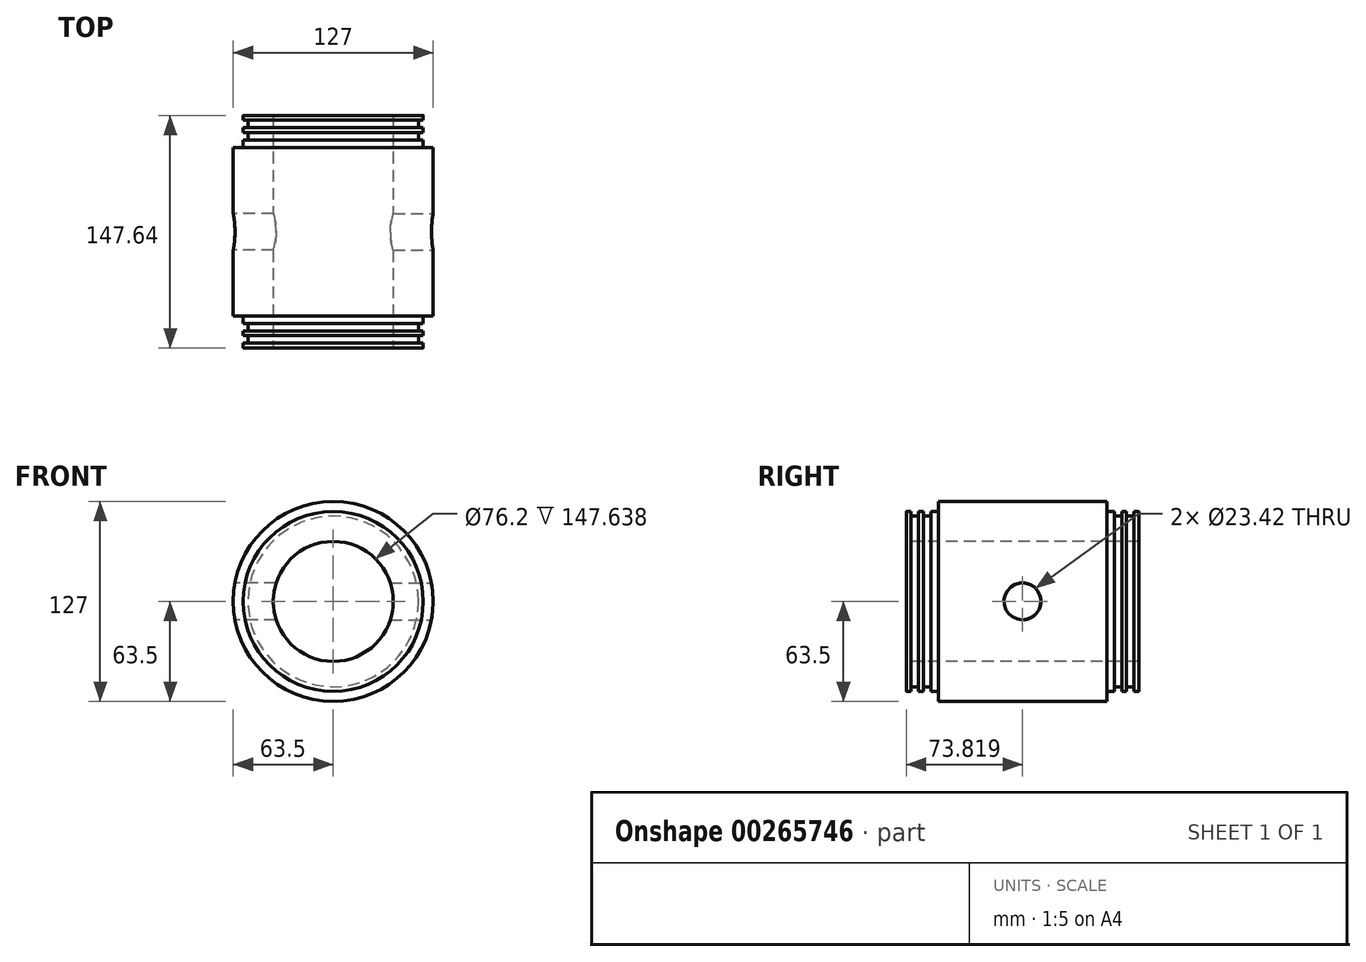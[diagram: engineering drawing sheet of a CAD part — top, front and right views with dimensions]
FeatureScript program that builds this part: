
annotation { "Feature Type Name" : "Feature", "Feature Type Description" : "" }
export const myFeature = defineFeature(function(context is Context, id is Id, definition is map)
    precondition{}
    {
        {
            var Q0;
            Q0=qCreatedBy(makeId("Right.planeOp"),FACE);
            var sketch = newSketch(context, id + "F0", { "sketchPlane" : qUnion([Q0])});
            skLineSegment(sketch, "E0", {"start": v(0, 0) * mm, "end": v(0, 57.15) * mm});
            skLineSegment(sketch, "E1", {"start": v(0, 57.15) * mm, "end": v(20.32, 57.15) * mm});
            skLineSegment(sketch, "E2", {"start": v(20.32, 57.15) * mm, "end": v(20.32, 63.5) * mm});
            skLineSegment(sketch, "E3", {"start": v(20.32, 63.5) * mm, "end": v(127.32, 63.5) * mm});
            skLineSegment(sketch, "E4", {"start": v(127.32, 63.5) * mm, "end": v(127.32, 57.15) * mm});
            skLineSegment(sketch, "E5", {"start": v(127.32, 57.15) * mm, "end": v(147.64, 57.15) * mm});
            skLineSegment(sketch, "E6", {"start": v(147.64, 57.15) * mm, "end": v(147.64, 0) * mm});
            skLineSegment(sketch, "E7", {"start": v(0, 0) * mm, "end": v(147.64, 0) * mm});
            skLineSegment(sketch, "E8", {"start": v(0, 57.15) * mm, "end": v(3.05, 57.15) * mm});
            skLineSegment(sketch, "E9", {"start": v(3.05, 57.15) * mm, "end": v(3.05, 54.15) * mm});
            skLineSegment(sketch, "E10", {"start": v(3.05, 54.15) * mm, "end": v(7.8, 54.15) * mm});
            skLineSegment(sketch, "E11", {"start": v(7.8, 54.15) * mm, "end": v(7.8, 57.15) * mm});
            skLineSegment(sketch, "E12", {"start": v(7.8, 57.15) * mm, "end": v(10.8, 57.15) * mm});
            skLineSegment(sketch, "E13", {"start": v(10.8, 57.15) * mm, "end": v(10.8, 54.15) * mm});
            skLineSegment(sketch, "E14", {"start": v(10.8, 54.15) * mm, "end": v(15.54, 54.15) * mm});
            skLineSegment(sketch, "E15", {"start": v(15.54, 54.15) * mm, "end": v(15.54, 57.15) * mm});
            skLineSegment(sketch, "E16", {"start": v(15.54, 57.15) * mm, "end": v(20.32, 57.15) * mm});
            skLineSegment(sketch, "E17", {"start": v(147.64, 57.15) * mm, "end": v(144.59, 57.15) * mm});
            skLineSegment(sketch, "E18", {"start": v(144.59, 57.15) * mm, "end": v(144.59, 54.15) * mm});
            skLineSegment(sketch, "E19", {"start": v(144.59, 54.15) * mm, "end": v(139.84, 54.15) * mm});
            skLineSegment(sketch, "E20", {"start": v(139.84, 54.15) * mm, "end": v(139.84, 57.15) * mm});
            skLineSegment(sketch, "E21", {"start": v(139.84, 57.15) * mm, "end": v(136.84, 57.15) * mm});
            skLineSegment(sketch, "E22", {"start": v(136.84, 57.15) * mm, "end": v(136.84, 54.15) * mm});
            skLineSegment(sketch, "E23", {"start": v(136.84, 54.15) * mm, "end": v(132.1, 54.15) * mm});
            skLineSegment(sketch, "E24", {"start": v(132.1, 54.15) * mm, "end": v(132.1, 57.15) * mm});
            skSolve(sketch);
        }
        {
            var Q0;
            Q0=makeQuery(id+"F0.imprint","IMPRINT",FACE,{"disambiguationData":[TD([[makeQuery(id+"F0.imprint","IMPRINT",EDGE,{"derivedFrom":sQuery(id+"F0.wireOp",EDGE,"E0")}),-1.0]])]});
            var Q1;
            Q1=sQuery(id+"F0.wireOp",EDGE,"E7");
            revolve(context, id + "F1", {"entities" : qUnion([Q0]), "axis" : qUnion([Q1]), "revolveType" : RevolveType.FULL});
        }
        {
            var Q0;
            Q0=makeQuery(id+"F1.opRevolve","SWEPT_FACE",FACE,{"disambiguationData":[OSD([sQuery(id+"F0.wireOp",EDGE,"E0")])]});
            var sketch = newSketch(context, id + "F2", { "sketchPlane" : qUnion([Q0])});
            skCircle(sketch, "E25", {"center": v(0, 0) * mm, "radius": 38.1 * mm});
            skSolve(sketch);
        }
        {
            var Q0;
            Q0=makeQuery(id+"F2.imprint","IMPRINT",FACE,{"disambiguationData":[TD([[makeQuery(id+"F2.imprint","IMPRINT",EDGE,{"derivedFrom":sQuery(id+"F2.wireOp",EDGE,"E25")}),1.0]])]});
            extrude(context, id + "F3", {"entities" : qUnion([Q0]), "operationType" : NewBodyOperationType.REMOVE, "endBound" : BoundingType.UP_TO_NEXT, "oppositeDirection" : true, "depth" : 25.4 * mm});
        }
        {
            var Q0;
            Q0=makeQuery(id+"F1.opRevolve","SWEPT_EDGE",EDGE,{"disambiguationData":[OSD([sQuery(id+"F0.wireOp",EDGE,"E0"),sQuery(id+"F0.wireOp",EDGE,"E8")])]});
            var Q1;
            Q1=makeQuery(id+"F1.opRevolve","SWEPT_EDGE",EDGE,{"disambiguationData":[OSD([sQuery(id+"F0.wireOp",EDGE,"E6"),sQuery(id+"F0.wireOp",EDGE,"E17")])]});
            fillet(context, id + "F4", {"entities" : qUnion([Q0, Q1]), "radius" : 0.13 * mm, "tangentPropagation" : true, "allowEdgeOverflow" : false});
        }
        {
            var Q0;
            Q0=qCreatedBy(makeId("Right.planeOp"),FACE);
            cPlane(context, id + "F5", {"entities" : qUnion([Q0]), "cplaneType" : CPlaneType.OFFSET, "offset" : 63.5 * mm, "width" : 152.4 * mm, "height" : 152.4 * mm});
        }
        {
            var Q0;
            Q0=qCreatedBy(id+"F5.planeOp",FACE);
            var sketch = newSketch(context, id + "F6", { "sketchPlane" : qUnion([Q0])});
            skPoint(sketch, "E26", {"position": v(73.82, 0) * mm});
            skSolve(sketch);
        }
        {
            var Q0;
            Q0=sQuery(id+"F6.wireOp",VERTEX,"E26");
            var Q1;
            Q1=makeQuery(id+"F1.opRevolve","SWEPT_BODY",BODY,{"disambiguationData":[OSD([sQuery(id+"F0.wireOp",EDGE,"E0"),sQuery(id+"F0.wireOp",EDGE,"E2"),sQuery(id+"F0.wireOp",EDGE,"E3"),sQuery(id+"F0.wireOp",EDGE,"E4"),sQuery(id+"F0.wireOp",EDGE,"E5"),sQuery(id+"F0.wireOp",EDGE,"E6"),sQuery(id+"F0.wireOp",EDGE,"E7"),sQuery(id+"F0.wireOp",EDGE,"E8"),sQuery(id+"F0.wireOp",EDGE,"E9"),sQuery(id+"F0.wireOp",EDGE,"E10"),sQuery(id+"F0.wireOp",EDGE,"E11"),sQuery(id+"F0.wireOp",EDGE,"E12"),sQuery(id+"F0.wireOp",EDGE,"E13"),sQuery(id+"F0.wireOp",EDGE,"E14"),sQuery(id+"F0.wireOp",EDGE,"E15"),sQuery(id+"F0.wireOp",EDGE,"E16"),sQuery(id+"F0.wireOp",EDGE,"E17"),sQuery(id+"F0.wireOp",EDGE,"E18"),sQuery(id+"F0.wireOp",EDGE,"E19"),sQuery(id+"F0.wireOp",EDGE,"E20"),sQuery(id+"F0.wireOp",EDGE,"E21"),sQuery(id+"F0.wireOp",EDGE,"E22"),sQuery(id+"F0.wireOp",EDGE,"E23"),sQuery(id+"F0.wireOp",EDGE,"E24")])]});
            hole(context, id + "F7", {"style" : HoleStyle.SIMPLE, "endStyle" : HoleEndStyle.BLIND, "standardTappedOrClearance" : lookupTablePath({ "standard" : "ANSI", "engagement" : "75%", "pitch" : "12 tpi", "size" : "1", "type" : "Tapped" }), "standardBlindInLast" : lookupTablePath({ "standard" : "ANSI", "engagement" : "75%", "pitch" : "12 tpi", "size" : "1", "type" : "Tapped" }), "holeDiameter" : 23.42 * mm, "showTappedDepth" : true, "holeDepth" : 38.1 * mm, "tappedDepth" : 31.75 * mm, "tapClearance" : 3, "locations" : qUnion([Q0]), "scope" : qUnion([Q1]), "majorDiameter" : 25.4 * mm});
        }
        {
            var Q0;
            Q0=qCreatedBy(makeId("Right.planeOp"),FACE);
            cPlane(context, id + "F8", {"entities" : qUnion([Q0]), "cplaneType" : CPlaneType.OFFSET, "offset" : 63.5 * mm, "oppositeDirection" : true, "width" : 152.4 * mm, "height" : 152.4 * mm});
        }
        {
            var Q0;
            Q0=qCreatedBy(id+"F8.planeOp",FACE);
            var sketch = newSketch(context, id + "F9", { "sketchPlane" : qUnion([Q0])});
            skPoint(sketch, "E27", {"position": v(73.82, 0) * mm});
            skSolve(sketch);
        }
        {
            var Q0;
            Q0=sQuery(id+"F9.wireOp",VERTEX,"E27");
            var Q1;
            Q1=makeQuery(id+"F1.opRevolve","SWEPT_BODY",BODY,{"disambiguationData":[OSD([sQuery(id+"F0.wireOp",EDGE,"E0"),sQuery(id+"F0.wireOp",EDGE,"E2"),sQuery(id+"F0.wireOp",EDGE,"E3"),sQuery(id+"F0.wireOp",EDGE,"E4"),sQuery(id+"F0.wireOp",EDGE,"E5"),sQuery(id+"F0.wireOp",EDGE,"E6"),sQuery(id+"F0.wireOp",EDGE,"E7"),sQuery(id+"F0.wireOp",EDGE,"E8"),sQuery(id+"F0.wireOp",EDGE,"E9"),sQuery(id+"F0.wireOp",EDGE,"E10"),sQuery(id+"F0.wireOp",EDGE,"E11"),sQuery(id+"F0.wireOp",EDGE,"E12"),sQuery(id+"F0.wireOp",EDGE,"E13"),sQuery(id+"F0.wireOp",EDGE,"E14"),sQuery(id+"F0.wireOp",EDGE,"E15"),sQuery(id+"F0.wireOp",EDGE,"E16"),sQuery(id+"F0.wireOp",EDGE,"E17"),sQuery(id+"F0.wireOp",EDGE,"E18"),sQuery(id+"F0.wireOp",EDGE,"E19"),sQuery(id+"F0.wireOp",EDGE,"E20"),sQuery(id+"F0.wireOp",EDGE,"E21"),sQuery(id+"F0.wireOp",EDGE,"E22"),sQuery(id+"F0.wireOp",EDGE,"E23"),sQuery(id+"F0.wireOp",EDGE,"E24")])]});
            hole(context, id + "F10", {"style" : HoleStyle.SIMPLE, "endStyle" : HoleEndStyle.BLIND, "oppositeDirection" : true, "standardTappedOrClearance" : lookupTablePath({ "standard" : "ANSI", "engagement" : "75%", "pitch" : "12 tpi", "size" : "1", "type" : "Tapped" }), "standardBlindInLast" : lookupTablePath({ "standard" : "ANSI", "engagement" : "75%", "pitch" : "12 tpi", "size" : "1", "type" : "Tapped" }), "holeDiameter" : 23.42 * mm, "showTappedDepth" : true, "holeDepth" : 38.1 * mm, "tappedDepth" : 31.75 * mm, "tapClearance" : 3, "locations" : qUnion([Q0]), "scope" : qUnion([Q1]), "majorDiameter" : 25.4 * mm});
        }
    });
